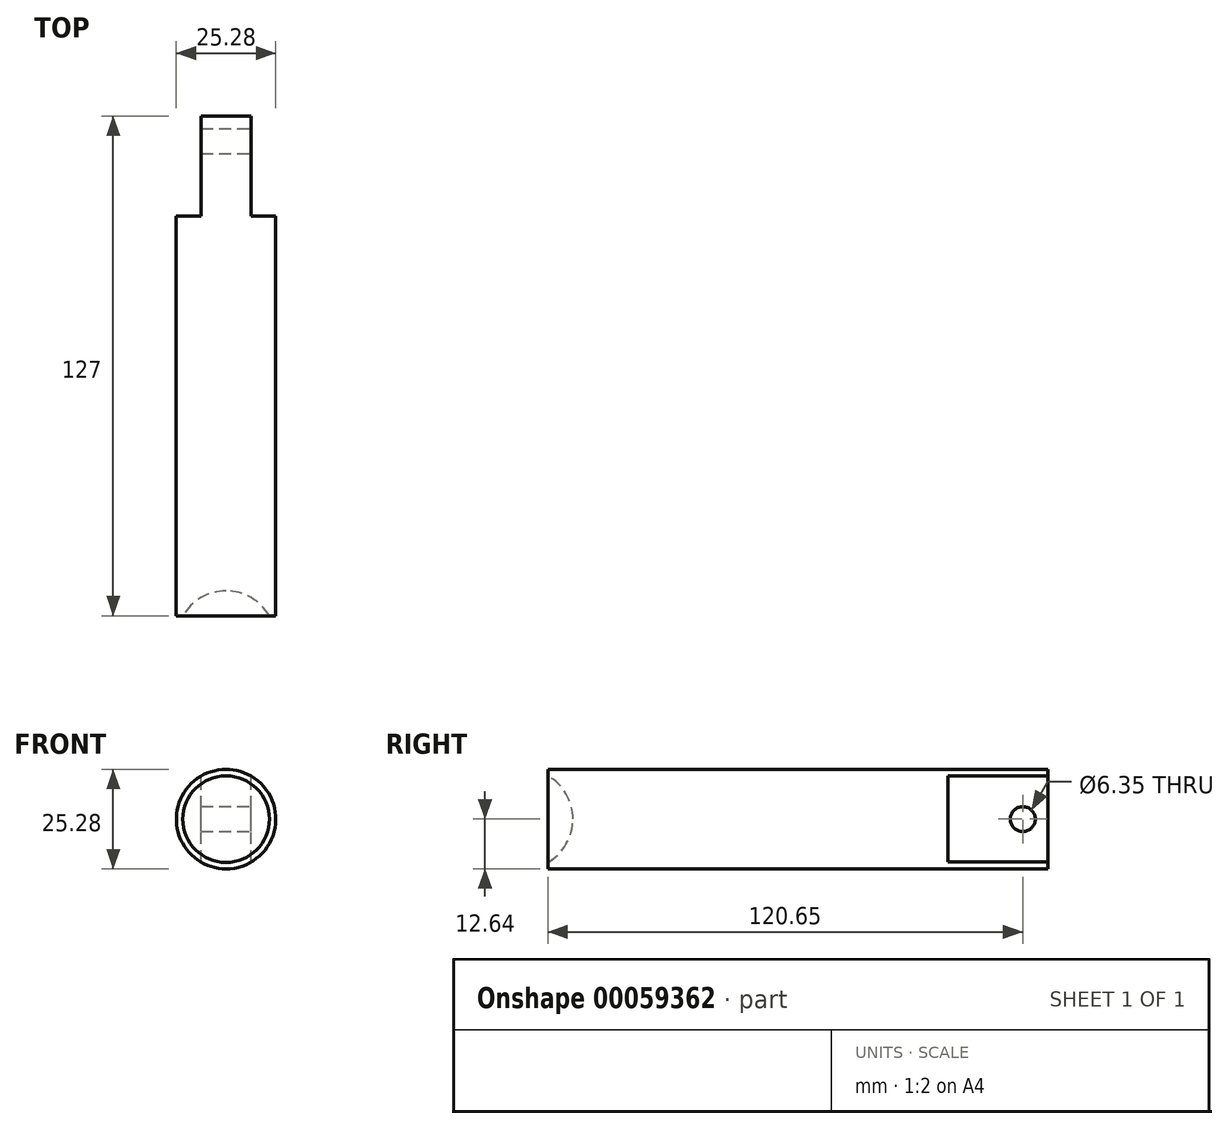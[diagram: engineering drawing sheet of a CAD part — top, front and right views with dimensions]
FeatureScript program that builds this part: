
annotation { "Feature Type Name" : "Feature", "Feature Type Description" : "" }
export const myFeature = defineFeature(function(context is Context, id is Id, definition is map)
    precondition{}
    {
        {
            var Q0;
            Q0=qCreatedBy(makeId("Front.planeOp"),FACE);
            var sketch = newSketch(context, id + "F0", { "sketchPlane" : qUnion([Q0])});
            skCircle(sketch, "E0", {"center": v(0, 0) * mm, "radius": 12.64 * mm});
            skSolve(sketch);
        }
        {
            var Q0;
            Q0=makeQuery(id+"F0.imprint","IMPRINT",FACE,{"disambiguationData":[TD([[makeQuery(id+"F0.imprint","IMPRINT",EDGE,{"derivedFrom":sQuery(id+"F0.wireOp",EDGE,"E0")}),1.0]])]});
            extrude(context, id + "F1", {"entities" : qUnion([Q0]), "depth" : 127 * mm});
        }
        {
            var Q0;
            Q0=qCreatedBy(makeId("Right.planeOp"),FACE);
            var sketch = newSketch(context, id + "F2", { "sketchPlane" : qUnion([Q0])});
            skArc(sketch, "E1", {"start": v(-120.65, 0) * mm, "mid": v(-124.37, 8.98) * mm, "end": v(-133.35, 12.7) * mm});
            skLineSegment(sketch, "E2", {"start": v(-133.35, 0) * mm, "end": v(-133.35, 12.7) * mm});
            skLineSegment(sketch, "E3", {"start": v(-133.35, 0) * mm, "end": v(-120.65, 0) * mm});
            skSolve(sketch);
        }
        {
            var Q0;
            Q0=makeQuery(id+"F2.imprint","IMPRINT",FACE,{"disambiguationData":[TD([[makeQuery(id+"F2.imprint","IMPRINT",EDGE,{"derivedFrom":sQuery(id+"F2.wireOp",EDGE,"E1")}),1.0]])]});
            var Q1;
            Q1=sQuery(id+"F2.wireOp",EDGE,"E3");
            revolve(context, id + "F3", {"operationType" : NewBodyOperationType.REMOVE, "entities" : qUnion([Q0]), "axis" : qUnion([Q1]), "revolveType" : RevolveType.FULL, "oppositeDirection" : true});
        }
        {
            var Q0;
            Q0=qCreatedBy(makeId("Top.planeOp"),FACE);
            var sketch = newSketch(context, id + "F4", { "sketchPlane" : qUnion([Q0])});
            skLineSegment(sketch, "E4.bottom", {"start": v(-34.18, -25.4) * mm, "end": v(-6.35, -25.4) * mm});
            skLineSegment(sketch, "E4.top", {"start": v(-34.18, 25.67) * mm, "end": v(-6.35, 25.67) * mm});
            skLineSegment(sketch, "E4.left", {"start": v(-34.18, -25.4) * mm, "end": v(-34.18, 25.67) * mm});
            skLineSegment(sketch, "E4.right", {"start": v(-6.35, -25.4) * mm, "end": v(-6.35, 25.67) * mm});
            skLineSegment(sketch, "E5.bottom", {"start": v(6.35, -25.4) * mm, "end": v(31.48, -25.4) * mm});
            skLineSegment(sketch, "E5.top", {"start": v(6.35, 19.75) * mm, "end": v(31.48, 19.75) * mm});
            skLineSegment(sketch, "E5.left", {"start": v(6.35, -25.4) * mm, "end": v(6.35, 19.75) * mm});
            skLineSegment(sketch, "E5.right", {"start": v(31.48, -25.4) * mm, "end": v(31.48, 19.75) * mm});
            skSolve(sketch);
        }
        {
            var Q0;
            Q0 = qSketchRegion(id + "F4", true);
            extrude(context, id + "F5", {"entities" : qUnion([Q0]), "operationType" : NewBodyOperationType.REMOVE, "endBound" : BoundingType.THROUGH_ALL, "oppositeDirection" : true, "depth" : 25.4 * mm, "hasSecondDirection" : true, "secondDirectionOppositeDirection" : false, "secondDirectionDepth" : 25.4 * mm});
        }
        {
            var Q0;
            Q0=qCreatedBy(makeId("Right.planeOp"),FACE);
            var sketch = newSketch(context, id + "F6", { "sketchPlane" : qUnion([Q0])});
            skCircle(sketch, "E6", {"center": v(-6.35, 0) * mm, "radius": 3.18 * mm});
            skSolve(sketch);
        }
        {
            var Q0;
            Q0 = qSketchRegion(id + "F6", true);
            extrude(context, id + "F7", {"entities" : qUnion([Q0]), "operationType" : NewBodyOperationType.REMOVE, "endBound" : BoundingType.THROUGH_ALL, "oppositeDirection" : true, "depth" : 25.4 * mm, "hasSecondDirection" : true, "secondDirectionOppositeDirection" : false, "secondDirectionDepth" : 25.4 * mm});
        }
    });
